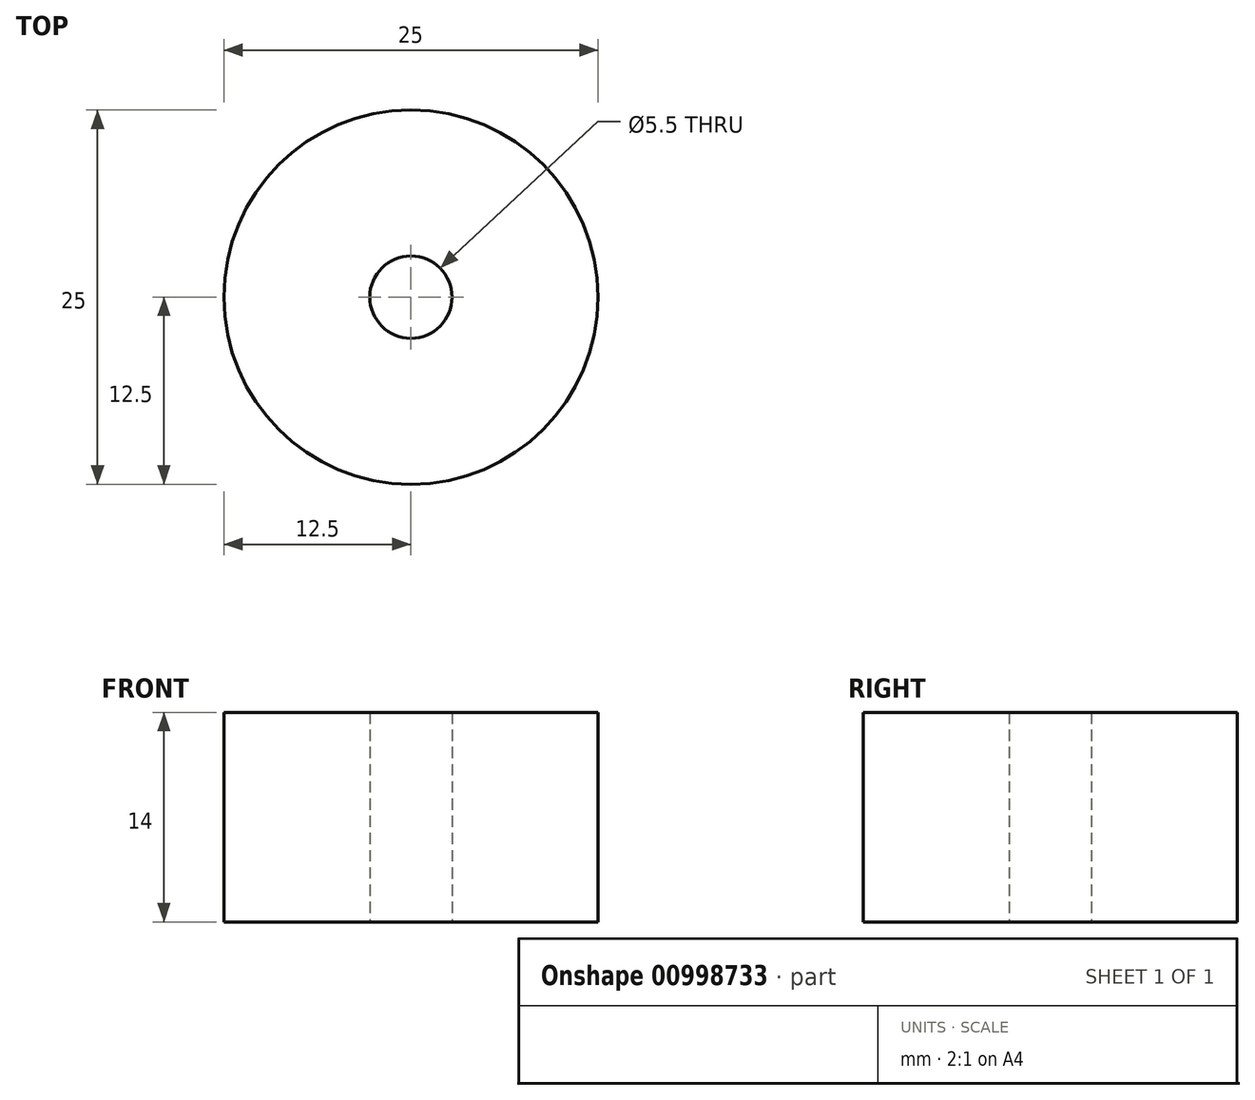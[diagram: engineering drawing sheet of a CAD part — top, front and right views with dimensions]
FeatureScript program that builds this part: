
annotation { "Feature Type Name" : "Feature", "Feature Type Description" : "" }
export const myFeature = defineFeature(function(context is Context, id is Id, definition is map)
    precondition{}
    {
        {
            var Q0;
            Q0=qCreatedBy(makeId("Top.planeOp"),FACE);
            var sketch = newSketch(context, id + "F0", { "sketchPlane" : qUnion([Q0])});
            skCircle(sketch, "E0", {"center": v(0, 0) * mm, "radius": 12.5 * mm});
            skCircle(sketch, "E1", {"center": v(0, 0) * mm, "radius": 2.75 * mm});
            skSolve(sketch);
        }
        {
            var Q0;
            Q0=makeQuery(id+"F0.imprint","IMPRINT",FACE,{"disambiguationData":[TD([[makeQuery(id+"F0.imprint","IMPRINT",EDGE,{"derivedFrom":sQuery(id+"F0.wireOp",EDGE,"E0")}),1.0]])]});
            extrude(context, id + "F1", {"entities" : qUnion([Q0]), "depth" : 14 * mm, "offsetDistance" : 25 * mm});
        }
    });
